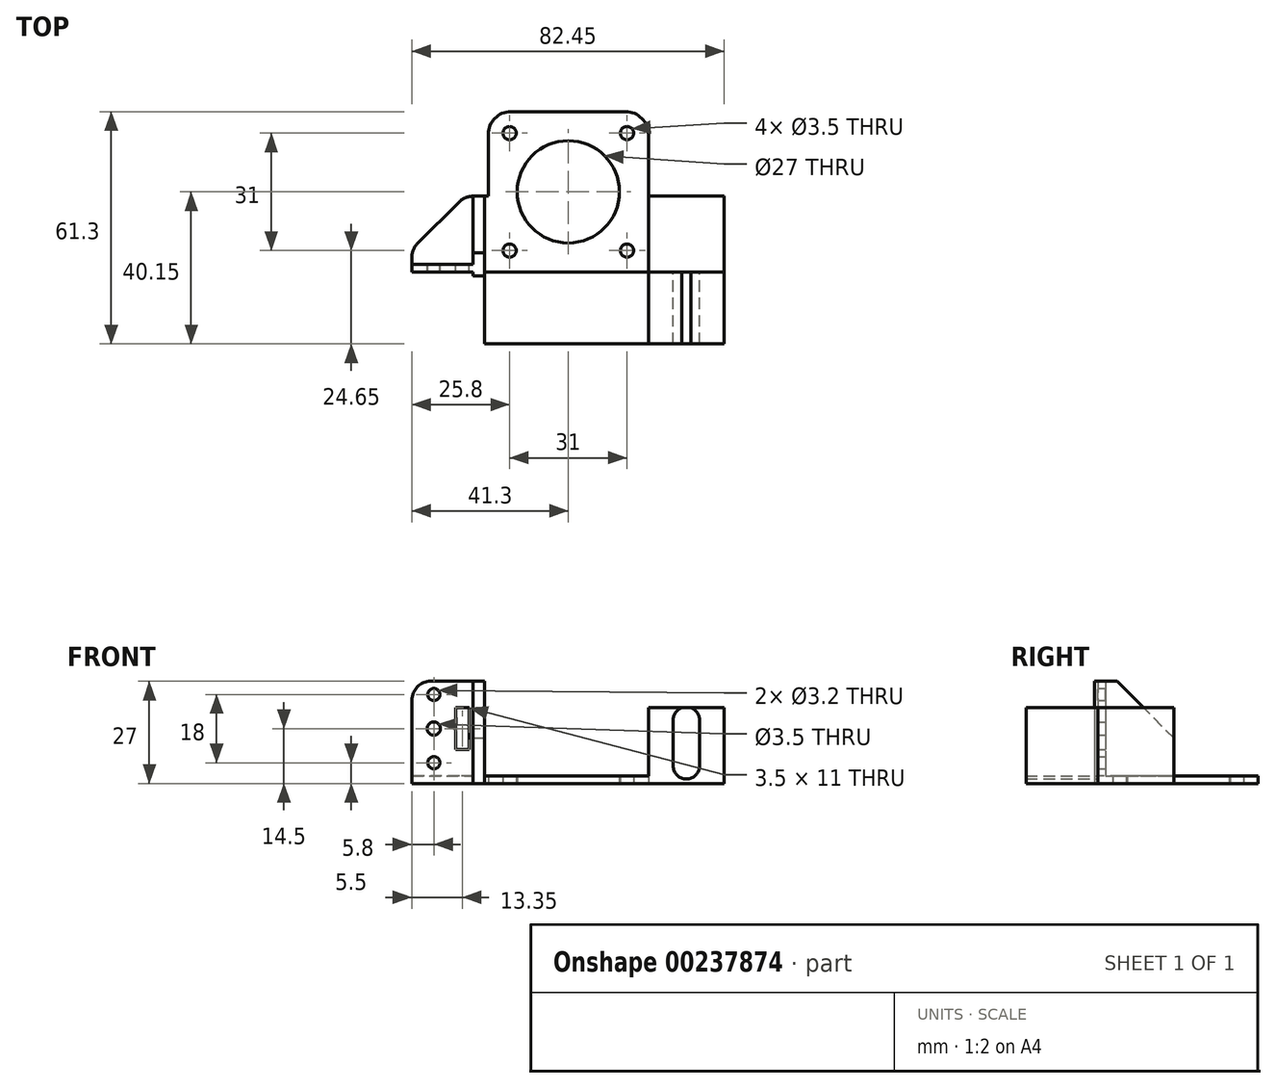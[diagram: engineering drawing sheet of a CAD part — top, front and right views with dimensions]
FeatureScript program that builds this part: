
annotation { "Feature Type Name" : "Feature", "Feature Type Description" : "" }
export const myFeature = defineFeature(function(context is Context, id is Id, definition is map)
    precondition{}
    {
        {
            var Q0;
            Q0=qCreatedBy(makeId("Top.planeOp"),FACE);
            var sketch = newSketch(context, id + "F0", { "sketchPlane" : qUnion([Q0])});
            skLineSegment(sketch, "E0.bottom", {"start": v(21.15, 21.15) * mm, "end": v(-21.15, 21.15) * mm});
            skLineSegment(sketch, "E0.top", {"start": v(21.15, -21.15) * mm, "end": v(-21.15, -21.15) * mm});
            skLineSegment(sketch, "E0.left", {"start": v(21.15, 21.15) * mm, "end": v(21.15, -21.15) * mm});
            skLineSegment(sketch, "E0.right", {"start": v(-21.15, 21.15) * mm, "end": v(-21.15, -21.15) * mm});
            skPoint(sketch, "E0.middle", {"position": v(0, 0) * mm});
            skLineSegment(sketch, "E1.bottom", {"start": v(15.5, 15.5) * mm, "end": v(-15.5, 15.5) * mm, "construction": true});
            skLineSegment(sketch, "E1.top", {"start": v(15.5, -15.5) * mm, "end": v(-15.5, -15.5) * mm, "construction": true});
            skLineSegment(sketch, "E1.left", {"start": v(15.5, 15.5) * mm, "end": v(15.5, -15.5) * mm, "construction": true});
            skLineSegment(sketch, "E1.right", {"start": v(-15.5, 15.5) * mm, "end": v(-15.5, -15.5) * mm, "construction": true});
            skCircle(sketch, "E2", {"center": v(-15.5, 15.5) * mm, "radius": 1.75 * mm});
            skCircle(sketch, "E3", {"center": v(15.5, 15.5) * mm, "radius": 1.75 * mm});
            skCircle(sketch, "E4", {"center": v(15.5, -15.5) * mm, "radius": 1.75 * mm});
            skCircle(sketch, "E5", {"center": v(-15.5, -15.5) * mm, "radius": 1.75 * mm});
            skCircle(sketch, "E6", {"center": v(0, 0) * mm, "radius": 13.5 * mm});
            skLineSegment(sketch, "E7.bottom", {"start": v(-21.15, -21.15) * mm, "end": v(-41.3, -21.15) * mm});
            skLineSegment(sketch, "E7.top", {"start": v(-21.15, -1.15) * mm, "end": v(-41.3, -1.15) * mm});
            skLineSegment(sketch, "E7.left", {"start": v(-21.15, -21.15) * mm, "end": v(-21.15, -1.15) * mm});
            skLineSegment(sketch, "E7.right", {"start": v(-41.3, -21.15) * mm, "end": v(-41.3, -1.15) * mm});
            skLineSegment(sketch, "E8.bottom", {"start": v(-41.3, -21.15) * mm, "end": v(-21.16, -21.15) * mm});
            skLineSegment(sketch, "E8.top", {"start": v(-41.3, -22.15) * mm, "end": v(-21.16, -22.15) * mm});
            skLineSegment(sketch, "E8.left", {"start": v(-41.3, -21.15) * mm, "end": v(-41.3, -22.15) * mm});
            skLineSegment(sketch, "E8.right", {"start": v(-21.16, -21.15) * mm, "end": v(-21.16, -22.15) * mm});
            skLineSegment(sketch, "E9", {"start": v(21.15, -1.15) * mm, "end": v(41.15, -1.15) * mm});
            skLineSegment(sketch, "E10", {"start": v(41.15, -1.15) * mm, "end": v(41.15, -21.15) * mm});
            skLineSegment(sketch, "E11", {"start": v(41.15, -21.15) * mm, "end": v(21.15, -21.15) * mm});
            skSolve(sketch);
        }
        {
            var Q0;
            Q0=makeQuery(id+"F0.imprint","IMPRINT",FACE,{"disambiguationData":[TD([[makeQuery(id+"F0.imprint","IMPRINT",EDGE,{"derivedFrom":sQuery(id+"F0.wireOp",EDGE,"E0.bottom")}),1.0]])]});
            var Q1;
            Q1=makeQuery(id+"F0.imprint","IMPRINT",FACE,{"disambiguationData":[TD([[makeQuery(id+"F0.imprint","IMPRINT",EDGE,{"derivedFrom":sQuery(id+"F0.wireOp",EDGE,"E7.bottom")}),-1.0]])]});
            var Q2;
            Q2=makeQuery(id+"F0.imprint","IMPRINT",FACE,{"disambiguationData":[TD([[makeQuery(id+"F0.imprint","IMPRINT",EDGE,{"derivedFrom":sQuery(id+"F0.wireOp",EDGE,"E8.bottom")}),-1.0]])]});
            var Q3;
            {var subQ2=sQuery(id+"F0.wireOp",EDGE,"E9");Q3=makeQuery(id+"F0.imprint","IMPRINT",FACE,{"disambiguationData":[TD([[makeQuery(id+"F0.imprint","IMPRINT",EDGE,{"derivedFrom":subQ2}),-1.0]])]});}
            extrude(context, id + "F1", {"entities" : qUnion([Q0, Q1, Q2, Q3]), "depth" : 2 * mm});
        }
        {
            var Q0;
            Q0=qCreatedBy(makeId("Top.planeOp"),FACE);
            var sketch = newSketch(context, id + "F2", { "sketchPlane" : qUnion([Q0])});
            skLineSegment(sketch, "E12.bottom", {"start": v(-22.16, -1.15) * mm, "end": v(-25.16, -1.15) * mm});
            skLineSegment(sketch, "E12.top", {"start": v(-22.16, -22.15) * mm, "end": v(-25.16, -22.15) * mm});
            skLineSegment(sketch, "E12.left", {"start": v(-22.16, -1.15) * mm, "end": v(-22.16, -22.15) * mm});
            skLineSegment(sketch, "E12.right", {"start": v(-25.16, -1.15) * mm, "end": v(-25.16, -22.15) * mm});
            skSolve(sketch);
        }
        {
            var Q0;
            Q0=qSketchRegion(id+"F2",true);
            extrude(context, id + "F3", {"entities" : qUnion([Q0]), "operationType" : NewBodyOperationType.ADD, "depth" : 27 * mm});
        }
        {
            var Q0;
            {var subQ0=sQuery(id+"F0.wireOp",EDGE,"E8.left");var subQ1=sQuery(id+"F0.wireOp",EDGE,"E7.right");var subQ2=sQuery(id+"F0.wireOp",EDGE,"E8.top");var subQ3=sQuery(id+"F0.wireOp",EDGE,"E7.top");Q0=makeQuery(id+"F3.boolean.opBoolean","SPLIT",FACE,{"disambiguationData":[TD([makeQuery(id+"F3.opExtrude","SWEPT_FACE",FACE,{"disambiguationData":[OSD([sQuery(id+"F2.wireOp",EDGE,"E12.right")])]})])],"derivedFrom":makeQuery(id+"F1.opExtrude","CAP_FACE",FACE,{"disambiguationData":[OSD([sQuery(id+"F0.wireOp",EDGE,"E0.bottom"),sQuery(id+"F0.wireOp",EDGE,"E0.top"),sQuery(id+"F0.wireOp",EDGE,"E0.left"),sQuery(id+"F0.wireOp",EDGE,"E0.right"),sQuery(id+"F0.wireOp",EDGE,"E2"),sQuery(id+"F0.wireOp",EDGE,"E3"),sQuery(id+"F0.wireOp",EDGE,"E4"),sQuery(id+"F0.wireOp",EDGE,"E5"),sQuery(id+"F0.wireOp",EDGE,"E6"),sQuery(id+"F0.wireOp",EDGE,"E7.bottom"),subQ3,subQ1,subQ2,subQ0,sQuery(id+"F0.wireOp",EDGE,"E8.right")])],"isStart":false})});}
            var sketch = newSketch(context, id + "F4", { "sketchPlane" : qUnion([Q0])});
            skLineSegment(sketch, "E13.bottom", {"start": v(-41.3, -19.15) * mm, "end": v(-25.16, -19.15) * mm});
            skLineSegment(sketch, "E13.top", {"start": v(-41.3, -22.15) * mm, "end": v(-25.16, -22.15) * mm});
            skLineSegment(sketch, "E13.left", {"start": v(-41.3, -19.15) * mm, "end": v(-41.3, -22.15) * mm});
            skLineSegment(sketch, "E13.right", {"start": v(-25.16, -19.15) * mm, "end": v(-25.16, -22.15) * mm});
            skSolve(sketch);
        }
        {
            var Q0;
            Q0=makeQuery(id+"F4.imprint","IMPRINT",FACE,{"disambiguationData":[TD([[makeQuery(id+"F4.imprint","IMPRINT",EDGE,{"derivedFrom":sQuery(id+"F4.wireOp",EDGE,"E13.bottom")}),-1.0]])]});
            extrude(context, id + "F5", {"entities" : qUnion([Q0]), "operationType" : NewBodyOperationType.ADD, "depth" : 25 * mm});
        }
        {
            var Q0;
            Q0=makeQuery(id+"F5.opExtrude","SWEPT_FACE",FACE,{"disambiguationData":[OSD([sQuery(id+"F4.wireOp",EDGE,"E13.bottom")])]});
            var sketch = newSketch(context, id + "F6", { "sketchPlane" : qUnion([Q0])});
            skCircle(sketch, "E14", {"center": v(35.5, 14.5) * mm, "radius": 1.75 * mm});
            skCircle(sketch, "E15", {"center": v(35.5, 5.5) * mm, "radius": 1.6 * mm});
            skCircle(sketch, "E16", {"center": v(35.5, 23.5) * mm, "radius": 1.6 * mm});
            skLineSegment(sketch, "E17.bottom", {"start": v(29.7, 20) * mm, "end": v(26.2, 20) * mm});
            skLineSegment(sketch, "E17.top", {"start": v(29.7, 9) * mm, "end": v(26.2, 9) * mm});
            skLineSegment(sketch, "E17.left", {"start": v(29.7, 20) * mm, "end": v(29.7, 9) * mm});
            skLineSegment(sketch, "E17.right", {"start": v(26.2, 20) * mm, "end": v(26.2, 9) * mm});
            skSolve(sketch);
        }
        {
            var Q0;
            Q0=makeQuery(id+"F6.imprint","IMPRINT",FACE,{"disambiguationData":[TD([[makeQuery(id+"F6.imprint","IMPRINT",EDGE,{"derivedFrom":sQuery(id+"F6.wireOp",EDGE,"E14")}),1.0]])]});
            var Q1;
            Q1=makeQuery(id+"F6.imprint","IMPRINT",FACE,{"disambiguationData":[TD([[makeQuery(id+"F6.imprint","IMPRINT",EDGE,{"derivedFrom":sQuery(id+"F6.wireOp",EDGE,"E15")}),1.0]])]});
            var Q2;
            Q2=makeQuery(id+"F6.imprint","IMPRINT",FACE,{"disambiguationData":[TD([[makeQuery(id+"F6.imprint","IMPRINT",EDGE,{"derivedFrom":sQuery(id+"F6.wireOp",EDGE,"E16")}),1.0]])]});
            var Q3;
            Q3=makeQuery(id+"F6.imprint","IMPRINT",FACE,{"disambiguationData":[TD([[makeQuery(id+"F6.imprint","IMPRINT",EDGE,{"derivedFrom":sQuery(id+"F6.wireOp",EDGE,"E17.bottom")}),1.0]])]});
            extrude(context, id + "F7", {"entities" : qUnion([Q0, Q1, Q2, Q3]), "operationType" : NewBodyOperationType.REMOVE, "oppositeDirection" : true, "depth" : 25 * mm});
        }
        {
            var Q0;
            Q0=makeQuery(id+"F3.opExtrude","CAP_EDGE",EDGE,{"disambiguationData":[OSD([sQuery(id+"F2.wireOp",EDGE,"E12.bottom")])],"isStart":false});
            chamfer(context, id + "F8", {"entities" : qUnion([Q0]), "width" : 15 * mm, "tangentPropagation" : true});
        }
        {
            var Q0;
            Q0=makeQuery(id+"F1.opExtrude","SWEPT_EDGE",EDGE,{"disambiguationData":[OSD([sQuery(id+"F0.wireOp",EDGE,"E7.top"),sQuery(id+"F0.wireOp",EDGE,"E7.right")])]});
            chamfer(context, id + "F9", {"entities" : qUnion([Q0]), "width" : 14 * mm, "tangentPropagation" : true});
        }
        {
            var Q0;
            {var subQ0=sQuery(id+"F0.wireOp",EDGE,"E7.right");Q0=makeQuery(id+"F9.opChamfer","BLEND_EDGE",EDGE,{"blendedFrom":[makeQuery(id+"F1.opExtrude","SWEPT_EDGE",EDGE,{"disambiguationData":[OSD([sQuery(id+"F0.wireOp",EDGE,"E7.top"),subQ0])]}),makeQuery(id+"F5.boolean.opBoolean","MERGE",FACE,{"derivedFrom":[makeQuery(id+"F1.opExtrude","SWEPT_FACE",FACE,{"disambiguationData":[OSD([subQ0,sQuery(id+"F0.wireOp",EDGE,"E8.left")])]}),makeQuery(id+"F5.opExtrude","SWEPT_FACE",FACE,{"disambiguationData":[OSD([sQuery(id+"F4.wireOp",EDGE,"E13.left")])]})]})],"blendedInto":[makeQuery(id+"F5.boolean.opBoolean","MERGE",FACE,{"derivedFrom":[makeQuery(id+"F1.opExtrude","SWEPT_FACE",FACE,{"disambiguationData":[OSD([subQ0,sQuery(id+"F0.wireOp",EDGE,"E8.left")])]}),makeQuery(id+"F5.opExtrude","SWEPT_FACE",FACE,{"disambiguationData":[OSD([sQuery(id+"F4.wireOp",EDGE,"E13.left")])]})]})]});}
            var Q1;
            {var subQ0=sQuery(id+"F0.wireOp",EDGE,"E7.top");Q1=makeQuery(id+"F9.opChamfer","BLEND_EDGE",EDGE,{"blendedFrom":[makeQuery(id+"F1.opExtrude","SWEPT_EDGE",EDGE,{"disambiguationData":[OSD([subQ0,sQuery(id+"F0.wireOp",EDGE,"E7.right")])]}),makeQuery(id+"F3.boolean.opBoolean","MERGE",FACE,{"derivedFrom":[makeQuery(id+"F1.opExtrude","SWEPT_FACE",FACE,{"disambiguationData":[OSD([subQ0])]}),makeQuery(id+"F3.opExtrude","SWEPT_FACE",FACE,{"disambiguationData":[OSD([sQuery(id+"F2.wireOp",EDGE,"E12.bottom")])]})]})],"blendedInto":[makeQuery(id+"F3.boolean.opBoolean","MERGE",FACE,{"derivedFrom":[makeQuery(id+"F1.opExtrude","SWEPT_FACE",FACE,{"disambiguationData":[OSD([subQ0])]}),makeQuery(id+"F3.opExtrude","SWEPT_FACE",FACE,{"disambiguationData":[OSD([sQuery(id+"F2.wireOp",EDGE,"E12.bottom")])]})]})]});}
            var Q2;
            Q2=makeQuery(id+"F1.opExtrude","SWEPT_EDGE",EDGE,{"disambiguationData":[OSD([sQuery(id+"F0.wireOp",EDGE,"E8.top"),sQuery(id+"F0.wireOp",EDGE,"E8.right")])]});
            var Q3;
            Q3=makeQuery(id+"F5.opExtrude","CAP_EDGE",EDGE,{"disambiguationData":[OSD([sQuery(id+"F4.wireOp",EDGE,"E13.left")])],"isStart":false});
            fillet(context, id + "F10", {"entities" : qUnion([Q0, Q1, Q2, Q3]), "radius" : 5 * mm, "tangentPropagation" : true, "allowEdgeOverflow" : false});
        }
        {
            var Q0;
            Q0=makeQuery(id+"F1.opExtrude","SWEPT_EDGE",EDGE,{"disambiguationData":[OSD([sQuery(id+"F0.wireOp",EDGE,"E0.bottom"),sQuery(id+"F0.wireOp",EDGE,"E0.left")])]});
            var Q1;
            Q1=makeQuery(id+"F1.opExtrude","SWEPT_EDGE",EDGE,{"disambiguationData":[OSD([sQuery(id+"F0.wireOp",EDGE,"E0.bottom"),sQuery(id+"F0.wireOp",EDGE,"E0.right")])]});
            fillet(context, id + "F11", {"entities" : qUnion([Q0, Q1]), "radius" : 6 * mm, "tangentPropagation" : true, "allowEdgeOverflow" : false});
        }
        {
            var Q0;
            {var subQ0=sQuery(id+"F0.wireOp",EDGE,"E7.top");var subQ1=sQuery(id+"F0.wireOp",EDGE,"E5");var subQ2=sQuery(id+"F0.wireOp",EDGE,"E10");var subQ3=sQuery(id+"F0.wireOp",EDGE,"E4");var subQ4=sQuery(id+"F0.wireOp",EDGE,"E3");var subQ5=sQuery(id+"F0.wireOp",EDGE,"E2");var subQ6=sQuery(id+"F0.wireOp",EDGE,"E0.bottom");var subQ7=sQuery(id+"F0.wireOp",EDGE,"E6");var subQ8=sQuery(id+"F0.wireOp",EDGE,"E11");var subQ9=sQuery(id+"F0.wireOp",EDGE,"E7.bottom");var subQ10=sQuery(id+"F0.wireOp",EDGE,"E0.top");var subQ11=sQuery(id+"F0.wireOp",EDGE,"E0.left");var subQ12=sQuery(id+"F0.wireOp",EDGE,"E0.right");var subQ13=sQuery(id+"F0.wireOp",EDGE,"E8.top");var subQ14=sQuery(id+"F0.wireOp",EDGE,"E8.right");var subQ15=sQuery(id+"F0.wireOp",EDGE,"E9");Q0=makeQuery(id+"F3.boolean.opBoolean","SPLIT",FACE,{"disambiguationData":[TD([makeQuery(id+"F1.opExtrude","SWEPT_FACE",FACE,{"disambiguationData":[OSD([subQ6])]})])],"derivedFrom":makeQuery(id+"F1.opExtrude","CAP_FACE",FACE,{"disambiguationData":[OSD([subQ6,subQ10,subQ11,subQ12,subQ5,subQ4,subQ3,subQ1,subQ7,subQ9,subQ0,sQuery(id+"F0.wireOp",EDGE,"E7.right"),subQ13,sQuery(id+"F0.wireOp",EDGE,"E8.left"),subQ14,subQ15,subQ2,subQ8])],"isStart":false})});}
            var sketch = newSketch(context, id + "F12", { "sketchPlane" : qUnion([Q0])});
            skLineSegment(sketch, "E18.bottom", {"start": v(21.15, -1.15) * mm, "end": v(41.15, -1.15) * mm});
            skLineSegment(sketch, "E18.top", {"start": v(21.15, -21.15) * mm, "end": v(41.15, -21.15) * mm});
            skLineSegment(sketch, "E18.left", {"start": v(21.15, -1.15) * mm, "end": v(21.15, -21.15) * mm});
            skLineSegment(sketch, "E18.right", {"start": v(41.15, -1.15) * mm, "end": v(41.15, -21.15) * mm});
            skSolve(sketch);
        }
        {
            var Q0;
            Q0=makeQuery(id+"F12.imprint","IMPRINT",FACE,{"disambiguationData":[TD([[makeQuery(id+"F12.imprint","IMPRINT",EDGE,{"derivedFrom":sQuery(id+"F12.wireOp",EDGE,"E18.bottom")}),-1.0]])]});
            extrude(context, id + "F13", {"entities" : qUnion([Q0]), "operationType" : NewBodyOperationType.ADD, "depth" : 18 * mm});
        }
        {
            var Q0;
            Q0=makeQuery(id+"F13.boolean.opBoolean","MERGE",FACE,{"derivedFrom":[makeQuery(id+"F1.opExtrude","SWEPT_FACE",FACE,{"disambiguationData":[OSD([sQuery(id+"F0.wireOp",EDGE,"E0.top"),sQuery(id+"F0.wireOp",EDGE,"E7.bottom"),sQuery(id+"F0.wireOp",EDGE,"E11")])]}),makeQuery(id+"F13.opExtrude","SWEPT_FACE",FACE,{"disambiguationData":[OSD([sQuery(id+"F12.wireOp",EDGE,"E18.top")])]})]});
            var sketch = newSketch(context, id + "F14", { "sketchPlane" : qUnion([Q0])});
            skPoint(sketch, "E19", {"position": v(31.17, 4.7) * mm});
            skLineSegment(sketch, "E20", {"start": v(31.17, 4.7) * mm, "end": v(31.17, 16.71) * mm});
            skArc(sketch, "E21.0.startCap", {"start": v(34.67, 4.7) * mm, "mid": v(31.17, 1.2) * mm, "end": v(27.67, 4.71) * mm});
            skArc(sketch, "E21.0.endCap", {"start": v(27.67, 16.71) * mm, "mid": v(31.17, 20.2) * mm, "end": v(34.67, 16.71) * mm});
            skLineSegment(sketch, "E21.0.left", {"start": v(27.67, 4.7) * mm, "end": v(27.67, 16.71) * mm});
            skLineSegment(sketch, "E21.0.right", {"start": v(34.67, 4.7) * mm, "end": v(34.67, 16.71) * mm});
            skSolve(sketch);
        }
        {
            var Q0;
            {var subQ0=sQuery(id+"F14.wireOp",EDGE,"E21.0.endCap");var subQ1=makeQuery(id+"F13.opExtrude","CAP_EDGE",EDGE,{"disambiguationData":[OSD([sQuery(id+"F12.wireOp",EDGE,"E18.top")])],"isStart":false});var subQ2=makeQuery(id+"F14.imprint","INTERSECT",VERTEX,{"disambiguationData":[OD(0.0)],"derivedFrom":[subQ1,subQ0]});Q0=makeQuery(id+"F14.imprint","IMPRINT",FACE,{"disambiguationData":[TD([[makeQuery(id+"F14.imprint","IMPRINT",EDGE,{"disambiguationData":[TD([[subQ2,-1.0]])],"derivedFrom":subQ0}),-1.0]])]});}
            var Q1;
            Q1=makeQuery(id+"F14.imprint","IMPRINT",FACE,{"disambiguationData":[TD([[makeQuery(id+"F14.imprint","IMPRINT",EDGE,{"derivedFrom":sQuery(id+"F14.wireOp",EDGE,"E21.0.startCap")}),-1.0]])]});
            extrude(context, id + "F15", {"entities" : qUnion([Q0, Q1]), "depth" : 19 * mm});
        }
    });
